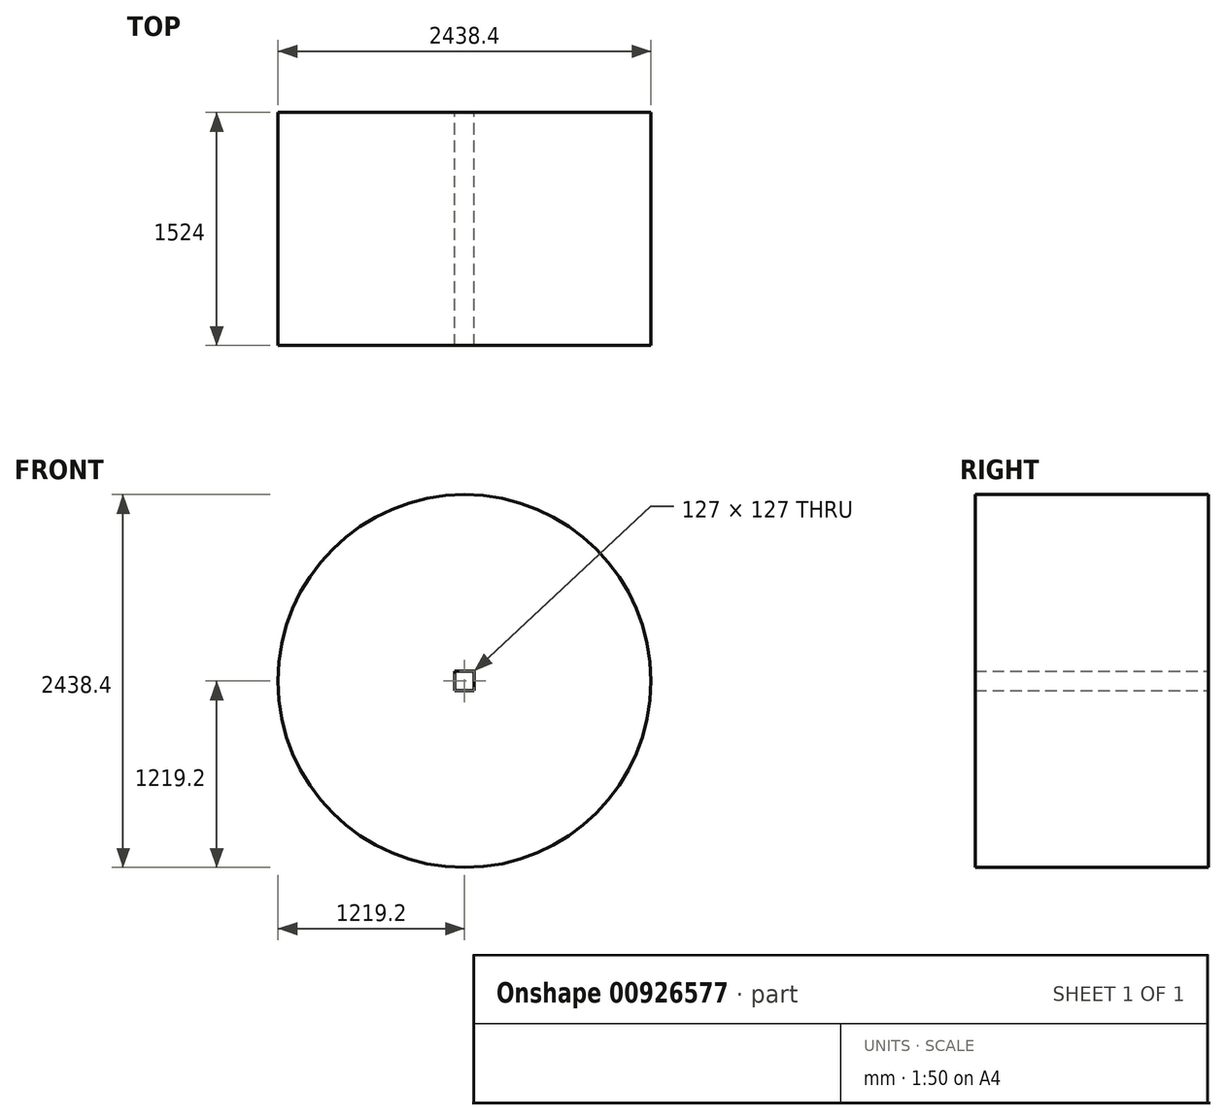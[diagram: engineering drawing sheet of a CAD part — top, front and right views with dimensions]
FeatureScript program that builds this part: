
annotation { "Feature Type Name" : "Feature", "Feature Type Description" : "" }
export const myFeature = defineFeature(function(context is Context, id is Id, definition is map)
    precondition{}
    {
        {
            var Q0;
            Q0=qCreatedBy(makeId("Front.planeOp"),FACE);
            var sketch = newSketch(context, id + "F0", { "sketchPlane" : qUnion([Q0])});
            skCircle(sketch, "E0", {"center": v(0, 0) * mm, "radius": 1219.2 * mm});
            skLineSegment(sketch, "E1.bottom", {"start": v(63.5, 63.5) * mm, "end": v(-63.5, 63.5) * mm});
            skLineSegment(sketch, "E1.top", {"start": v(63.5, -63.5) * mm, "end": v(-63.5, -63.5) * mm});
            skLineSegment(sketch, "E1.left", {"start": v(63.5, 63.5) * mm, "end": v(63.5, -63.5) * mm});
            skLineSegment(sketch, "E1.right", {"start": v(-63.5, 63.5) * mm, "end": v(-63.5, -63.5) * mm});
            skSolve(sketch);
        }
        {
            var Q0;
            Q0=makeQuery(id+"F0.imprint","IMPRINT",FACE,{"disambiguationData":[TD([[makeQuery(id+"F0.imprint","IMPRINT",EDGE,{"derivedFrom":sQuery(id+"F0.wireOp",EDGE,"E0")}),1.0]])]});
            extrude(context, id + "F1", {"entities" : qUnion([Q0]), "depth" : 1524 * mm, "offsetDistance" : 25.4 * mm});
        }
    });
